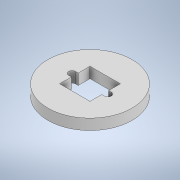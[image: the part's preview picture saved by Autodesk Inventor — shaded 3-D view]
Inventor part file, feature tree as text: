
AUTODESK INVENTOR PART (.ipt)
format: ipt  version: 2020 (Build 240168000, 168)  size: 119,296 bytes
history: native  units: mm
features: other x1, extrude x1, sketch x1
ambient origin geometry x8: Origin, YZ Plane, XZ Plane, XY Plane, X Axis, Y Axis, Z Axis, Center Point
bodies: Body1 (feature_tree)
feature tree (3):
  other  "Твердое тело1"
  extrude  "Выдавливание1"  Depth=17.0mm
  sketch  "Эскиз1"
